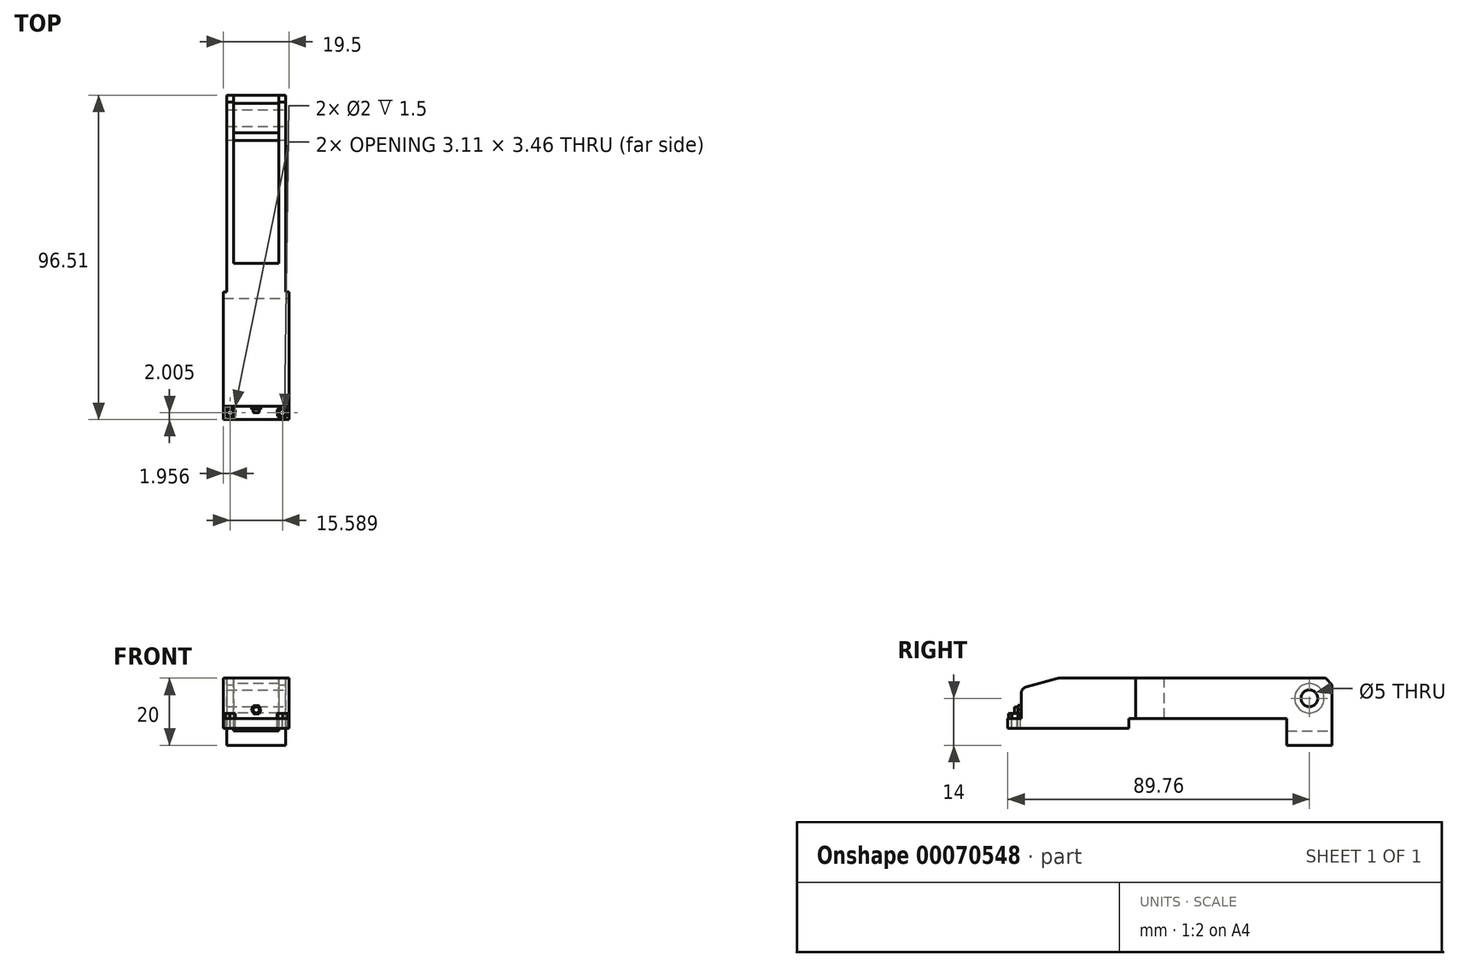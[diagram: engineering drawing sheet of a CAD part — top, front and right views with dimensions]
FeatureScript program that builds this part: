
annotation { "Feature Type Name" : "Feature", "Feature Type Description" : "" }
export const myFeature = defineFeature(function(context is Context, id is Id, definition is map)
    precondition{}
    {
        {
            var Q0;
            Q0=qCreatedBy(makeId("Right.planeOp"),FACE);
            var sketch = newSketch(context, id + "F0", { "sketchPlane" : qUnion([Q0])});
            skLineSegment(sketch, "E0", {"start": v(-14.69, 0) * mm, "end": v(-14.69, 12) * mm});
            skLineSegment(sketch, "E1", {"start": v(-14.69, 12) * mm, "end": v(77.82, 12) * mm});
            skLineSegment(sketch, "E2", {"start": v(77.82, 12) * mm, "end": v(77.82, -8) * mm});
            skLineSegment(sketch, "E3", {"start": v(77.82, -8) * mm, "end": v(64.31, -8) * mm});
            skLineSegment(sketch, "E4", {"start": v(64.31, -8) * mm, "end": v(64.31, 0) * mm});
            skLineSegment(sketch, "E5", {"start": v(64.31, 0) * mm, "end": v(-14.69, 0) * mm});
            skSolve(sketch);
        }
        {
            var Q0;
            Q0 = qSketchRegion(id + "F0", true);
            extrude(context, id + "F1", {"entities" : qUnion([Q0]), "depth" : 17.5 * mm});
        }
        {
            var Q0;
            Q0=makeQuery(id+"F1.opExtrude","SWEPT_FACE",FACE,{"disambiguationData":[OSD([sQuery(id+"F0.wireOp",EDGE,"E2")])]});
            var sketch = newSketch(context, id + "F2", { "sketchPlane" : qUnion([Q0])});
            skLineSegment(sketch, "E6", {"start": v(-15.5, -3.7) * mm, "end": v(-2, -3.7) * mm});
            skLineSegment(sketch, "E7", {"start": v(-2, -3.7) * mm, "end": v(-2, 12) * mm});
            skLineSegment(sketch, "E8", {"start": v(-2, 12) * mm, "end": v(-15.5, 12) * mm});
            skLineSegment(sketch, "E9", {"start": v(-15.5, 12) * mm, "end": v(-15.5, -3.7) * mm});
            skSolve(sketch);
        }
        {
            var Q0;
            Q0 = qSketchRegion(id + "F2", true);
            extrude(context, id + "F3", {"entities" : qUnion([Q0]), "operationType" : NewBodyOperationType.REMOVE, "oppositeDirection" : true, "depth" : 50 * mm});
        }
        {
            var Q0;
            Q0=makeQuery(id+"F1.opExtrude","CAP_FACE",FACE,{"disambiguationData":[OSD([sQuery(id+"F0.wireOp",EDGE,"E0"),sQuery(id+"F0.wireOp",EDGE,"E1"),sQuery(id+"F0.wireOp",EDGE,"E2"),sQuery(id+"F0.wireOp",EDGE,"E3"),sQuery(id+"F0.wireOp",EDGE,"E4"),sQuery(id+"F0.wireOp",EDGE,"E5")])],"isStart":true});
            var sketch = newSketch(context, id + "F4", { "sketchPlane" : qUnion([Q0])});
            skLineSegment(sketch, "E10.bottom", {"start": v(14.69, 12) * mm, "end": v(-19.31, 12) * mm});
            skLineSegment(sketch, "E10.top", {"start": v(14.69, 0) * mm, "end": v(-19.31, 0) * mm});
            skLineSegment(sketch, "E10.left", {"start": v(14.69, 12) * mm, "end": v(14.69, 0) * mm});
            skLineSegment(sketch, "E10.right", {"start": v(-19.31, 12) * mm, "end": v(-19.31, 0) * mm});
            skSolve(sketch);
        }
        {
            var Q0;
            Q0 = qSketchRegion(id + "F4", true);
            extrude(context, id + "F5", {"entities" : qUnion([Q0]), "operationType" : NewBodyOperationType.ADD, "depth" : 1 * mm});
        }
        {
            var Q0;
            Q0=makeQuery(id+"F1.opExtrude","CAP_FACE",FACE,{"disambiguationData":[OSD([sQuery(id+"F0.wireOp",EDGE,"E0"),sQuery(id+"F0.wireOp",EDGE,"E1"),sQuery(id+"F0.wireOp",EDGE,"E2"),sQuery(id+"F0.wireOp",EDGE,"E3"),sQuery(id+"F0.wireOp",EDGE,"E4"),sQuery(id+"F0.wireOp",EDGE,"E5")])],"isStart":false});
            var sketch = newSketch(context, id + "F6", { "sketchPlane" : qUnion([Q0])});
            skLineSegment(sketch, "E11.bottom", {"start": v(-14.69, 0) * mm, "end": v(19.31, 0) * mm});
            skLineSegment(sketch, "E11.top", {"start": v(-14.69, 12) * mm, "end": v(19.31, 12) * mm});
            skLineSegment(sketch, "E11.left", {"start": v(-14.69, 0) * mm, "end": v(-14.69, 12) * mm});
            skLineSegment(sketch, "E11.right", {"start": v(19.31, 0) * mm, "end": v(19.31, 12) * mm});
            skSolve(sketch);
        }
        {
            var Q0;
            Q0 = qSketchRegion(id + "F6", true);
            extrude(context, id + "F7", {"entities" : qUnion([Q0]), "operationType" : NewBodyOperationType.ADD, "depth" : 1 * mm});
        }
        {
            var Q0;
            Q0=makeQuery(id+"F1.opExtrude","SWEPT_EDGE",EDGE,{"disambiguationData":[OSD([sQuery(id+"F0.wireOp",EDGE,"E0"),sQuery(id+"F0.wireOp",EDGE,"E1")])]});
            chamfer(context, id + "F8", {"entities" : qUnion([Q0]), "chamferType" : ChamferType.TWO_OFFSETS, "width1" : 3 * mm, "oppositeDirection" : false, "width2" : 11 * mm, "tangentPropagation" : true});
        }
        {
            var Q0;
            {var subQ0=sQuery(id+"F0.wireOp",EDGE,"E1");Q0=makeQuery(id+"F8.opChamfer","BLEND_EDGE",EDGE,{"blendedFrom":[makeQuery(id+"F1.opExtrude","SWEPT_EDGE",EDGE,{"disambiguationData":[OSD([sQuery(id+"F0.wireOp",EDGE,"E0"),subQ0])]}),makeQuery(id+"F1.opExtrude","SWEPT_FACE",FACE,{"disambiguationData":[OSD([subQ0])]})],"blendedInto":[makeQuery(id+"F1.opExtrude","SWEPT_FACE",FACE,{"disambiguationData":[OSD([subQ0])]})]});}
            var Q1;
            {var subQ0=sQuery(id+"F0.wireOp",EDGE,"E0");Q1=makeQuery(id+"F8.opChamfer","BLEND_EDGE",EDGE,{"blendedFrom":[makeQuery(id+"F1.opExtrude","SWEPT_EDGE",EDGE,{"disambiguationData":[OSD([subQ0,sQuery(id+"F0.wireOp",EDGE,"E1")])]}),makeQuery(id+"F1.opExtrude","SWEPT_FACE",FACE,{"disambiguationData":[OSD([subQ0])]})],"blendedInto":[makeQuery(id+"F1.opExtrude","SWEPT_FACE",FACE,{"disambiguationData":[OSD([subQ0])]})]});}
            fillet(context, id + "F9", {"entities" : qUnion([Q0, Q1]), "radius" : 2 * mm, "tangentPropagation" : true, "allowEdgeOverflow" : false});
        }
        {
            var Q0;
            {var subQ0=sQuery(id+"F0.wireOp",EDGE,"E2");var subQ1=sQuery(id+"F0.wireOp",EDGE,"E1");Q0=makeQuery(id+"F3.boolean.opBoolean","SPLIT",EDGE,{"disambiguationData":[TD([makeQuery(id+"F3.opExtrude","SWEPT_FACE",FACE,{"disambiguationData":[OSD([sQuery(id+"F2.wireOp",EDGE,"E7")])]})])],"derivedFrom":makeQuery(id+"F1.opExtrude","SWEPT_EDGE",EDGE,{"disambiguationData":[OSD([subQ1,subQ0])]})});}
            var Q1;
            {var subQ0=sQuery(id+"F0.wireOp",EDGE,"E2");var subQ1=sQuery(id+"F0.wireOp",EDGE,"E1");Q1=makeQuery(id+"F3.boolean.opBoolean","SPLIT",EDGE,{"disambiguationData":[TD([makeQuery(id+"F3.opExtrude","SWEPT_FACE",FACE,{"disambiguationData":[OSD([sQuery(id+"F2.wireOp",EDGE,"E9")])]})])],"derivedFrom":makeQuery(id+"F1.opExtrude","SWEPT_EDGE",EDGE,{"disambiguationData":[OSD([subQ1,subQ0])]})});}
            chamfer(context, id + "F10", {"entities" : qUnion([Q0, Q1]), "width" : 2 * mm, "tangentPropagation" : true});
        }
        {
            var Q0;
            Q0=makeQuery(id+"F1.opExtrude","CAP_FACE",FACE,{"disambiguationData":[OSD([sQuery(id+"F0.wireOp",EDGE,"E0"),sQuery(id+"F0.wireOp",EDGE,"E1"),sQuery(id+"F0.wireOp",EDGE,"E2"),sQuery(id+"F0.wireOp",EDGE,"E3"),sQuery(id+"F0.wireOp",EDGE,"E4"),sQuery(id+"F0.wireOp",EDGE,"E5")])],"isStart":true});
            var sketch = newSketch(context, id + "F11", { "sketchPlane" : qUnion([Q0])});
            skLineSegment(sketch, "E12", {"start": v(-19.31, 6) * mm, "end": v(-82.95, 6) * mm, "construction": true});
            skLineSegment(sketch, "E13", {"start": v(-71.07, -8) * mm, "end": v(-71.07, 16.23) * mm, "construction": true});
            skCircle(sketch, "E14", {"center": v(-71.07, 6) * mm, "radius": 4.36 * mm});
            skPoint(sketch, "E14.centerSnap0", {"position": v(-71.07, 4.12) * mm});
            skSolve(sketch);
        }
        {
            var Q0;
            Q0 = qSketchRegion(id + "F11", true);
            extrude(context, id + "F12", {"entities" : qUnion([Q0]), "operationType" : NewBodyOperationType.ADD, "oppositeDirection" : true, "depth" : 17 * mm});
        }
        {
            var Q0;
            Q0=makeQuery(id+"F1.opExtrude","CAP_FACE",FACE,{"disambiguationData":[OSD([sQuery(id+"F0.wireOp",EDGE,"E0"),sQuery(id+"F0.wireOp",EDGE,"E1"),sQuery(id+"F0.wireOp",EDGE,"E2"),sQuery(id+"F0.wireOp",EDGE,"E3"),sQuery(id+"F0.wireOp",EDGE,"E4"),sQuery(id+"F0.wireOp",EDGE,"E5")])],"isStart":false});
            var sketch = newSketch(context, id + "F13", { "sketchPlane" : qUnion([Q0])});
            skLineSegment(sketch, "E15", {"start": v(71.07, -8) * mm, "end": v(71.07, 17.82) * mm, "construction": true});
            skLineSegment(sketch, "E16", {"start": v(19.31, 6) * mm, "end": v(84.14, 6) * mm, "construction": true});
            skCircle(sketch, "E17", {"center": v(71.07, 6) * mm, "radius": 2.5 * mm});
            skSolve(sketch);
        }
        {
            var Q0;
            Q0 = qSketchRegion(id + "F13", true);
            extrude(context, id + "F14", {"entities" : qUnion([Q0]), "operationType" : NewBodyOperationType.REMOVE, "oppositeDirection" : true, "depth" : 25 * mm});
        }
        {
            var Q0;
            Q0=makeQuery(id+"F7.boolean.opBoolean","MERGE",FACE,{"derivedFrom":[makeQuery(id+"F5.boolean.opBoolean","MERGE",FACE,{"derivedFrom":[makeQuery(id+"F1.opExtrude","SWEPT_FACE",FACE,{"disambiguationData":[OSD([sQuery(id+"F0.wireOp",EDGE,"E5")])]}),makeQuery(id+"F5.opExtrude","SWEPT_FACE",FACE,{"disambiguationData":[OSD([sQuery(id+"F4.wireOp",EDGE,"E10.top")])]})]}),makeQuery(id+"F7.opExtrude","SWEPT_FACE",FACE,{"disambiguationData":[OSD([sQuery(id+"F6.wireOp",EDGE,"E11.bottom")])]})]});
            var sketch = newSketch(context, id + "F15", { "sketchPlane" : qUnion([Q0])});
            skLineSegment(sketch, "E18.bottom", {"start": v(-1, 14.69) * mm, "end": v(18.5, 14.69) * mm});
            skLineSegment(sketch, "E18.top", {"start": v(-1, -17.36) * mm, "end": v(18.5, -17.36) * mm});
            skLineSegment(sketch, "E18.left", {"start": v(-1, 14.69) * mm, "end": v(-1, -17.36) * mm});
            skLineSegment(sketch, "E18.right", {"start": v(18.5, 14.69) * mm, "end": v(18.5, -17.36) * mm});
            skSolve(sketch);
        }
        {
            var Q0;
            Q0 = qSketchRegion(id + "F15", true);
            extrude(context, id + "F16", {"entities" : qUnion([Q0]), "operationType" : NewBodyOperationType.ADD, "depth" : 3 * mm});
        }
        {
            var Q0;
            Q0=makeQuery(id+"F16.boolean.opBoolean","MERGE",FACE,{"derivedFrom":[makeQuery(id+"F7.boolean.opBoolean","MERGE",FACE,{"derivedFrom":[makeQuery(id+"F5.boolean.opBoolean","MERGE",FACE,{"derivedFrom":[makeQuery(id+"F1.opExtrude","SWEPT_FACE",FACE,{"disambiguationData":[OSD([sQuery(id+"F0.wireOp",EDGE,"E0")])]}),makeQuery(id+"F5.opExtrude","SWEPT_FACE",FACE,{"disambiguationData":[OSD([sQuery(id+"F4.wireOp",EDGE,"E10.left")])]})]}),makeQuery(id+"F7.opExtrude","SWEPT_FACE",FACE,{"disambiguationData":[OSD([sQuery(id+"F6.wireOp",EDGE,"E11.left")])]})]}),makeQuery(id+"F16.opExtrude","SWEPT_FACE",FACE,{"disambiguationData":[OSD([sQuery(id+"F15.wireOp",EDGE,"E18.bottom")])]})]});
            var sketch = newSketch(context, id + "F17", { "sketchPlane" : qUnion([Q0])});
            skLineSegment(sketch, "E19.bottom", {"start": v(18.5, -3) * mm, "end": v(-1, -3) * mm});
            skLineSegment(sketch, "E19.top", {"start": v(18.5, 0) * mm, "end": v(-1, 0) * mm});
            skLineSegment(sketch, "E19.left", {"start": v(18.5, -3) * mm, "end": v(18.5, 0) * mm});
            skLineSegment(sketch, "E19.right", {"start": v(-1, -3) * mm, "end": v(-1, 0) * mm});
            skSolve(sketch);
        }
        {
            var Q0;
            Q0 = qSketchRegion(id + "F17", true);
            extrude(context, id + "F18", {"entities" : qUnion([Q0]), "operationType" : NewBodyOperationType.ADD, "depth" : 4 * mm});
        }
        {
            var Q0;
            Q0=makeQuery(id+"F18.opExtrude","SWEPT_FACE",FACE,{"disambiguationData":[OSD([sQuery(id+"F17.wireOp",EDGE,"E19.top")])]});
            var sketch = newSketch(context, id + "F19", { "sketchPlane" : qUnion([Q0])});
            skLineSegment(sketch, "E20", {"start": v(18.5, -16.69) * mm, "end": v(-3.4, -16.69) * mm, "construction": true});
            skPoint(sketch, "E20.endSnap0", {"position": v(-1, -16.69) * mm});
            skLineSegment(sketch, "E21", {"start": v(8.75, -18.69) * mm, "end": v(8.75, 0.44) * mm, "construction": true});
            skPoint(sketch, "E21.endSnap0", {"position": v(8.75, -14.69) * mm});
            skCircle(sketch, "E22.cCircle", {"center": v(16.54, -16.69) * mm, "radius": 1.5 * mm, "construction": true});
            skLineSegment(sketch, "E22.0", {"start": v(18.1, -17.45) * mm, "end": v(16.66, -18.41) * mm});
            skLineSegment(sketch, "E22.1", {"start": v(16.66, -18.41) * mm, "end": v(15.1, -17.65) * mm});
            skLineSegment(sketch, "E22.2", {"start": v(15.1, -17.65) * mm, "end": v(14.99, -15.92) * mm});
            skLineSegment(sketch, "E22.3", {"start": v(14.99, -15.92) * mm, "end": v(16.43, -14.96) * mm});
            skLineSegment(sketch, "E22.4", {"start": v(16.43, -14.96) * mm, "end": v(17.98, -15.72) * mm});
            skLineSegment(sketch, "E22.5", {"start": v(17.98, -15.72) * mm, "end": v(18.1, -17.45) * mm});
            skPoint(sketch, "E22.0.midPoint", {"position": v(17.38, -17.93) * mm});
            skLineSegment(sketch, "E23.MirrorCS", {"start": v(2.51, -15.92) * mm, "end": v(1.07, -14.96) * mm});
            skLineSegment(sketch, "E24.MirrorCS", {"start": v(1.07, -14.96) * mm, "end": v(-0.48, -15.72) * mm});
            skLineSegment(sketch, "E25.MirrorCS", {"start": v(-0.48, -15.72) * mm, "end": v(-0.6, -17.45) * mm});
            skLineSegment(sketch, "E26.MirrorCS", {"start": v(-0.6, -17.45) * mm, "end": v(0.84, -18.41) * mm});
            skLineSegment(sketch, "E27.MirrorCS", {"start": v(0.84, -18.41) * mm, "end": v(2.4, -17.65) * mm});
            skLineSegment(sketch, "E28.MirrorCS", {"start": v(2.4, -17.65) * mm, "end": v(2.51, -15.92) * mm});
            skSolve(sketch);
        }
        {
            var Q0;
            Q0 = qSketchRegion(id + "F19", true);
            extrude(context, id + "F20", {"entities" : qUnion([Q0]), "operationType" : NewBodyOperationType.REMOVE, "oppositeDirection" : true, "depth" : 25 * mm});
        }
        {
            var Q0;
            Q0=makeQuery(id+"F16.boolean.opBoolean","MERGE",FACE,{"derivedFrom":[makeQuery(id+"F7.boolean.opBoolean","MERGE",FACE,{"derivedFrom":[makeQuery(id+"F5.boolean.opBoolean","MERGE",FACE,{"derivedFrom":[makeQuery(id+"F1.opExtrude","SWEPT_FACE",FACE,{"disambiguationData":[OSD([sQuery(id+"F0.wireOp",EDGE,"E0")])]}),makeQuery(id+"F5.opExtrude","SWEPT_FACE",FACE,{"disambiguationData":[OSD([sQuery(id+"F4.wireOp",EDGE,"E10.left")])]})]}),makeQuery(id+"F7.opExtrude","SWEPT_FACE",FACE,{"disambiguationData":[OSD([sQuery(id+"F6.wireOp",EDGE,"E11.left")])]})]}),makeQuery(id+"F16.opExtrude","SWEPT_FACE",FACE,{"disambiguationData":[OSD([sQuery(id+"F15.wireOp",EDGE,"E18.bottom")])]})]});
            var sketch = newSketch(context, id + "F21", { "sketchPlane" : qUnion([Q0])});
            skLineSegment(sketch, "E29", {"start": v(8.75, 0) * mm, "end": v(8.75, 0) * mm});
            skPoint(sketch, "E29.endSnap0", {"position": v(8.75, 7.47) * mm});
            skCircle(sketch, "E30.cCircle", {"center": v(8.75, 2.56) * mm, "radius": 1.25 * mm, "construction": true});
            skLineSegment(sketch, "E30.0", {"start": v(7.31, 2.41) * mm, "end": v(7.9, 3.73) * mm});
            skLineSegment(sketch, "E30.1", {"start": v(7.9, 3.73) * mm, "end": v(9.33, 3.89) * mm});
            skLineSegment(sketch, "E30.2", {"start": v(9.33, 3.89) * mm, "end": v(10.19, 2.72) * mm});
            skLineSegment(sketch, "E30.3", {"start": v(10.19, 2.72) * mm, "end": v(9.6, 1.4) * mm});
            skLineSegment(sketch, "E30.4", {"start": v(9.6, 1.4) * mm, "end": v(8.17, 1.24) * mm});
            skLineSegment(sketch, "E30.5", {"start": v(8.17, 1.24) * mm, "end": v(7.31, 2.41) * mm});
            skPoint(sketch, "E30.0.midPoint", {"position": v(7.6, 3.07) * mm});
            skLineSegment(sketch, "E31", {"start": v(8.75, 0) * mm, "end": v(8.75, 7.47) * mm, "construction": true});
            skSolve(sketch);
        }
        {
            var Q0;
            Q0 = qSketchRegion(id + "F21", true);
            extrude(context, id + "F22", {"entities" : qUnion([Q0]), "operationType" : NewBodyOperationType.ADD, "depth" : 1 * mm});
        }
        {
            var Q0;
            Q0=makeQuery(id+"F22.opExtrude","CAP_FACE",FACE,{"disambiguationData":[OSD([sQuery(id+"F21.wireOp",EDGE,"E30.0"),sQuery(id+"F21.wireOp",EDGE,"E30.1"),sQuery(id+"F21.wireOp",EDGE,"E30.2"),sQuery(id+"F21.wireOp",EDGE,"E30.3"),sQuery(id+"F21.wireOp",EDGE,"E30.4"),sQuery(id+"F21.wireOp",EDGE,"E30.5")])],"isStart":false});
            var sketch = newSketch(context, id + "F23", { "sketchPlane" : qUnion([Q0])});
            skLineSegment(sketch, "E32", {"start": v(8.88, 1.32) * mm, "end": v(8.62, 3.8) * mm, "construction": true});
            skLineSegment(sketch, "E33", {"start": v(9.76, 3.3) * mm, "end": v(7.6, 1.73) * mm, "construction": true});
            skPoint(sketch, "E33.endSnap0", {"position": v(7.6, 3.07) * mm});
            skLineSegment(sketch, "E34", {"start": v(7.6, 1.73) * mm, "end": v(7.72, 2) * mm, "construction": true});
            skCircle(sketch, "E35", {"center": v(8.75, 2.56) * mm, "radius": 0.9 * mm});
            skSolve(sketch);
        }
        {
            var Q0;
            Q0 = qSketchRegion(id + "F23", true);
            extrude(context, id + "F24", {"entities" : qUnion([Q0]), "operationType" : NewBodyOperationType.ADD, "depth" : 1 * mm});
        }
        {
            var Q0;
            Q0 = qSketchRegion(id + "F19", true);
            extrude(context, id + "F25", {"entities" : qUnion([Q0]), "depth" : 1.5 * mm});
        }
        {
            var Q0;
            Q0=makeQuery(id+"F25.opExtrude","CAP_FACE",FACE,{"disambiguationData":[OSD([sQuery(id+"F19.wireOp",EDGE,"E22.0"),sQuery(id+"F19.wireOp",EDGE,"E22.1"),sQuery(id+"F19.wireOp",EDGE,"E22.2"),sQuery(id+"F19.wireOp",EDGE,"E22.3"),sQuery(id+"F19.wireOp",EDGE,"E22.4"),sQuery(id+"F19.wireOp",EDGE,"E22.5")])],"isStart":false});
            var sketch = newSketch(context, id + "F26", { "sketchPlane" : qUnion([Q0])});
            skLineSegment(sketch, "E36", {"start": v(16.66, -18.41) * mm, "end": v(16.43, -14.96) * mm, "construction": true});
            skLineSegment(sketch, "E37", {"start": v(14.99, -15.92) * mm, "end": v(18.1, -17.45) * mm, "construction": true});
            skLineSegment(sketch, "E38", {"start": v(18.1, -17.45) * mm, "end": v(18.11, -17.32) * mm, "construction": true});
            skCircle(sketch, "E39", {"center": v(16.54, -16.69) * mm, "radius": 1 * mm});
            skSolve(sketch);
        }
        {
            var Q0;
            Q0 = qSketchRegion(id + "F26", true);
            extrude(context, id + "F27", {"entities" : qUnion([Q0]), "operationType" : NewBodyOperationType.REMOVE, "oppositeDirection" : true, "depth" : 25 * mm});
        }
        {
            var Q0;
            Q0=makeQuery(id+"F25.opExtrude","CAP_FACE",FACE,{"disambiguationData":[OSD([sQuery(id+"F19.wireOp",EDGE,"E23.MirrorCS"),sQuery(id+"F19.wireOp",EDGE,"E24.MirrorCS"),sQuery(id+"F19.wireOp",EDGE,"E25.MirrorCS"),sQuery(id+"F19.wireOp",EDGE,"E26.MirrorCS"),sQuery(id+"F19.wireOp",EDGE,"E27.MirrorCS"),sQuery(id+"F19.wireOp",EDGE,"E28.MirrorCS")])],"isStart":false});
            var sketch = newSketch(context, id + "F28", { "sketchPlane" : qUnion([Q0])});
            skLineSegment(sketch, "E40", {"start": v(0.84, -18.41) * mm, "end": v(1.07, -14.96) * mm, "construction": true});
            skLineSegment(sketch, "E41", {"start": v(-0.48, -15.72) * mm, "end": v(2.4, -17.65) * mm, "construction": true});
            skCircle(sketch, "E42", {"center": v(0.96, -16.69) * mm, "radius": 1 * mm});
            skSolve(sketch);
        }
        {
            var Q0;
            Q0 = qSketchRegion(id + "F28", true);
            extrude(context, id + "F29", {"entities" : qUnion([Q0]), "operationType" : NewBodyOperationType.REMOVE, "oppositeDirection" : true, "depth" : 25 * mm});
        }
    });
